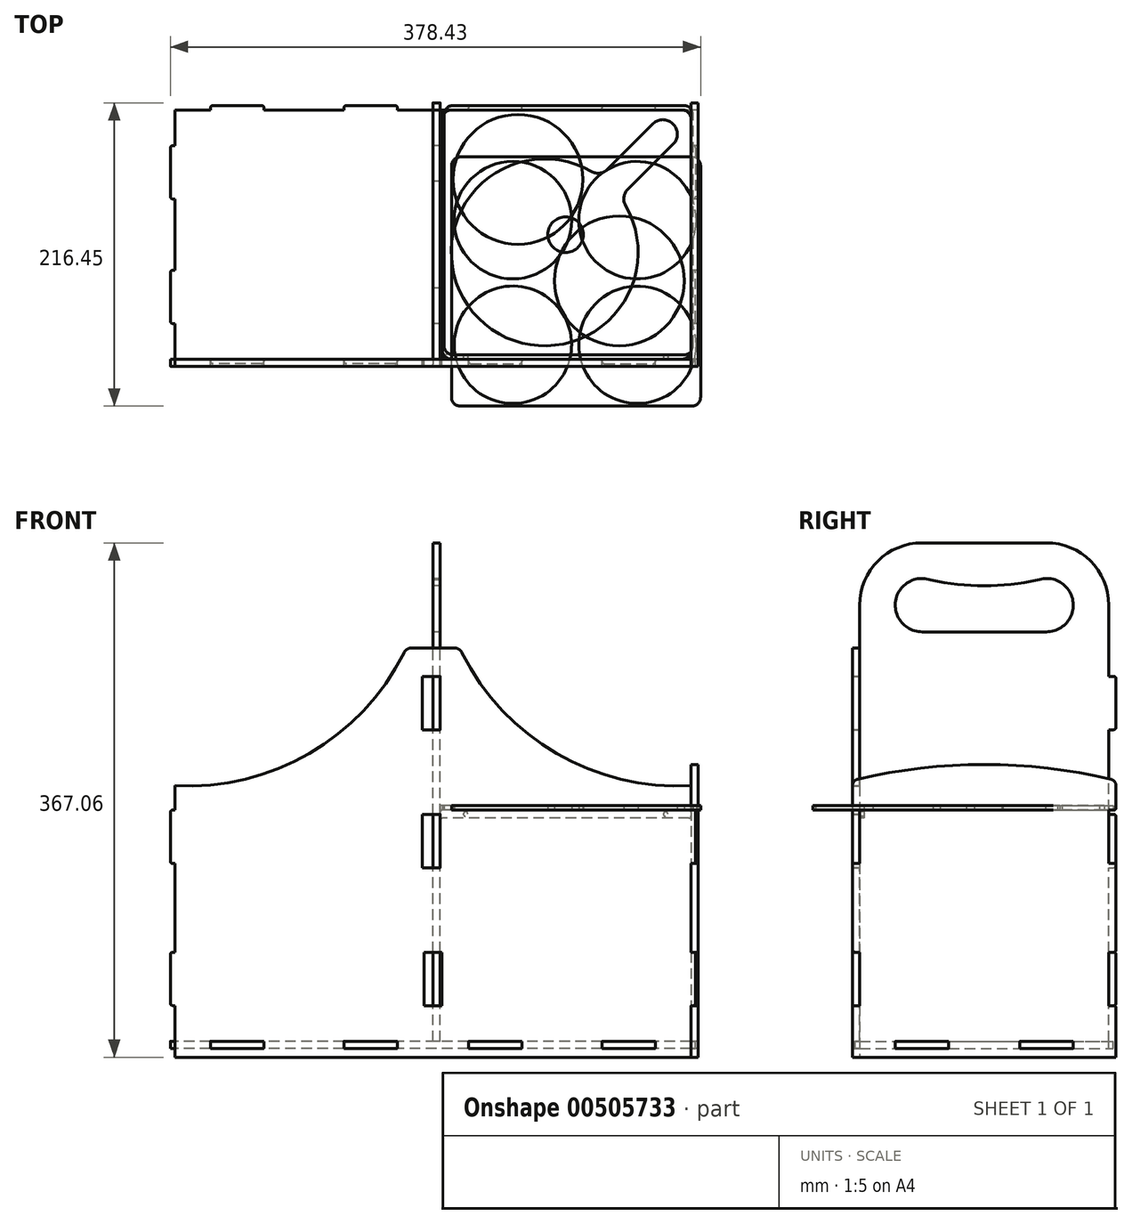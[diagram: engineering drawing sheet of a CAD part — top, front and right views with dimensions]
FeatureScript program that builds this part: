
annotation { "Feature Type Name" : "Feature", "Feature Type Description" : "" }
export const myFeature = defineFeature(function(context is Context, id is Id, definition is map)
    precondition{}
    {
        {
            var Q0;
            Q0=qCreatedBy(makeId("Right.planeOp"),FACE);
            var sketch = newSketch(context, id + "F0", { "sketchPlane" : qUnion([Q0])});
            skLineSegment(sketch, "E0.bottom", {"start": v(-88.9, 0) * mm, "end": v(88.9, 0) * mm});
            skLineSegment(sketch, "E0.top", {"start": v(-44.45, 355.6) * mm, "end": v(44.45, 355.6) * mm});
            skLineSegment(sketch, "E0.left", {"start": v(-88.9, 0) * mm, "end": v(-88.9, 25.4) * mm});
            skLineSegment(sketch, "E0.right", {"start": v(88.9, 0) * mm, "end": v(88.9, 25.4) * mm});
            skArc(sketch, "E1", {"start": v(-38.14, 329.13) * mm, "mid": v(-63.24, 314.26) * mm, "end": v(-44.27, 292.1) * mm});
            skArc(sketch, "E2", {"start": v(44.27, 292.1) * mm, "mid": v(63.24, 314.26) * mm, "end": v(38.14, 329.13) * mm});
            skPoint(sketch, "E3", {"position": v(-38.14, 329.13) * mm});
            skPoint(sketch, "E4", {"position": v(38.14, 329.13) * mm});
            skArc(sketch, "E5", {"start": v(-38.14, 329.13) * mm, "mid": v(0, 324.96) * mm, "end": v(38.14, 329.13) * mm});
            skLineSegment(sketch, "E6", {"start": v(-44.27, 292.1) * mm, "end": v(44.63, 292.1) * mm});
            skArc(sketch, "E7", {"start": v(88.9, 311.15) * mm, "mid": v(75.88, 342.58) * mm, "end": v(44.45, 355.6) * mm});
            skArc(sketch, "E8", {"start": v(-88.9, 311.15) * mm, "mid": v(-75.88, 342.58) * mm, "end": v(-44.45, 355.6) * mm});
            skLineSegment(sketch, "E9.top", {"start": v(94.01, 26.99) * mm, "end": v(94.01, 61.91) * mm});
            skLineSegment(sketch, "E9.left", {"start": v(88.9, 25.4) * mm, "end": v(92.42, 25.4) * mm});
            skLineSegment(sketch, "E9.right", {"start": v(88.9, 63.5) * mm, "end": v(92.42, 63.5) * mm});
            skPoint(sketch, "E10.visualSharp", {"position": v(94.01, 25.4) * mm});
            skArc(sketch, "E10.filletArc", {"start": v(92.42, 25.4) * mm, "mid": v(93.55, 25.86) * mm, "end": v(94.01, 26.99) * mm});
            skPoint(sketch, "E11.visualSharp", {"position": v(94.01, 63.5) * mm});
            skArc(sketch, "E11.filletArc", {"start": v(94.01, 61.91) * mm, "mid": v(93.55, 63.04) * mm, "end": v(92.42, 63.5) * mm});
            skLineSegment(sketch, "E12.top", {"start": v(94.01, 223.84) * mm, "end": v(94.01, 258.76) * mm});
            skLineSegment(sketch, "E12.left", {"start": v(88.9, 222.25) * mm, "end": v(92.42, 222.25) * mm});
            skLineSegment(sketch, "E12.right", {"start": v(88.9, 260.35) * mm, "end": v(92.42, 260.35) * mm});
            skPoint(sketch, "E13.visualSharp", {"position": v(94.01, 222.25) * mm});
            skArc(sketch, "E13.filletArc", {"start": v(92.42, 222.25) * mm, "mid": v(93.55, 222.71) * mm, "end": v(94.01, 223.84) * mm});
            skPoint(sketch, "E14.visualSharp", {"position": v(94.01, 260.35) * mm});
            skArc(sketch, "E14.filletArc", {"start": v(94.01, 258.76) * mm, "mid": v(93.55, 259.89) * mm, "end": v(92.42, 260.35) * mm});
            skLineSegment(sketch, "E15.top", {"start": v(94.01, 125.41) * mm, "end": v(94.01, 160.34) * mm});
            skLineSegment(sketch, "E15.left", {"start": v(88.9, 123.83) * mm, "end": v(92.42, 123.83) * mm});
            skLineSegment(sketch, "E15.right", {"start": v(88.9, 161.93) * mm, "end": v(92.42, 161.93) * mm});
            skPoint(sketch, "E16.visualSharp", {"position": v(94.01, 123.83) * mm});
            skArc(sketch, "E16.filletArc", {"start": v(92.42, 123.83) * mm, "mid": v(93.55, 124.29) * mm, "end": v(94.01, 125.41) * mm});
            skPoint(sketch, "E17.visualSharp", {"position": v(94.01, 161.93) * mm});
            skArc(sketch, "E17.filletArc", {"start": v(94.01, 160.34) * mm, "mid": v(93.55, 161.46) * mm, "end": v(92.42, 161.93) * mm});
            skArc(sketch, "E18.MirrorCS", {"start": v(-92.42, 25.4) * mm, "mid": v(-93.55, 25.86) * mm, "end": v(-94.01, 26.99) * mm});
            skLineSegment(sketch, "E19.MirrorCS", {"start": v(-88.9, 25.4) * mm, "end": v(-92.42, 25.4) * mm});
            skLineSegment(sketch, "E20.MirrorCS", {"start": v(-88.9, 161.93) * mm, "end": v(-92.42, 161.93) * mm});
            skArc(sketch, "E21.MirrorCS", {"start": v(-92.42, 222.25) * mm, "mid": v(-93.55, 222.71) * mm, "end": v(-94.01, 223.84) * mm});
            skArc(sketch, "E22.MirrorCS", {"start": v(-94.01, 258.76) * mm, "mid": v(-93.55, 259.89) * mm, "end": v(-92.42, 260.35) * mm});
            skLineSegment(sketch, "E23.MirrorCS", {"start": v(-88.9, 63.5) * mm, "end": v(-92.42, 63.5) * mm});
            skArc(sketch, "E24.MirrorCS", {"start": v(-94.01, 61.91) * mm, "mid": v(-93.55, 63.04) * mm, "end": v(-92.42, 63.5) * mm});
            skArc(sketch, "E25.MirrorCS", {"start": v(-94.01, 160.34) * mm, "mid": v(-93.55, 161.46) * mm, "end": v(-92.42, 161.93) * mm});
            skArc(sketch, "E26.MirrorCS", {"start": v(-92.42, 123.83) * mm, "mid": v(-93.55, 124.29) * mm, "end": v(-94.01, 125.41) * mm});
            skLineSegment(sketch, "E27.MirrorCS", {"start": v(-88.9, 222.25) * mm, "end": v(-92.42, 222.25) * mm});
            skLineSegment(sketch, "E28.MirrorCS", {"start": v(-88.9, 123.83) * mm, "end": v(-92.42, 123.83) * mm});
            skLineSegment(sketch, "E29.MirrorCS", {"start": v(-88.9, 260.35) * mm, "end": v(-92.42, 260.35) * mm});
            skPoint(sketch, "E30.MirrorP", {"position": v(-94.01, 260.35) * mm});
            skPoint(sketch, "E31.MirrorP", {"position": v(-94.01, 63.5) * mm});
            skPoint(sketch, "E32.MirrorP", {"position": v(-94.01, 25.4) * mm});
            skLineSegment(sketch, "E33.MirrorCS", {"start": v(-94.01, 125.41) * mm, "end": v(-94.01, 160.34) * mm});
            skPoint(sketch, "E34.MirrorP", {"position": v(-94.01, 161.93) * mm});
            skPoint(sketch, "E35.MirrorP", {"position": v(-94.01, 123.83) * mm});
            skPoint(sketch, "E36.MirrorP", {"position": v(-94.01, 222.25) * mm});
            skLineSegment(sketch, "E37.MirrorCS", {"start": v(-94.01, 223.84) * mm, "end": v(-94.01, 258.76) * mm});
            skLineSegment(sketch, "E38.MirrorCS", {"start": v(-94.01, 26.99) * mm, "end": v(-94.01, 61.91) * mm});
            skLineSegment(sketch, "E39.trimOffspring", {"start": v(88.9, 260.35) * mm, "end": v(88.9, 311.15) * mm});
            skLineSegment(sketch, "E40.trimOffspring", {"start": v(-88.9, 260.35) * mm, "end": v(-88.9, 311.15) * mm});
            skLineSegment(sketch, "E41.trimOffspring", {"start": v(-88.9, 161.93) * mm, "end": v(-88.9, 222.25) * mm});
            skLineSegment(sketch, "E42.trimOffspring", {"start": v(88.9, 161.93) * mm, "end": v(88.9, 222.25) * mm});
            skLineSegment(sketch, "E43.trimOffspring", {"start": v(-88.9, 63.5) * mm, "end": v(-88.9, 123.83) * mm});
            skLineSegment(sketch, "E44.trimOffspring", {"start": v(88.9, 63.5) * mm, "end": v(88.9, 123.83) * mm});
            skSolve(sketch);
        }
        {
            var Q0;
            Q0=makeQuery(id+"F0.imprint","IMPRINT",FACE,{"disambiguationData":[TD([[makeQuery(id+"F0.imprint","IMPRINT",EDGE,{"derivedFrom":sQuery(id+"F0.wireOp",EDGE,"E0.bottom")}),1.0]])]});
            extrude(context, id + "F1", {"entities" : qUnion([Q0]), "depth" : 5.11 * mm, "offsetDistance" : 25.4 * mm});
        }
        {
            var Q0;
            Q0=qCreatedBy(makeId("Top.planeOp"),FACE);
            var sketch = newSketch(context, id + "F2", { "sketchPlane" : qUnion([Q0])});
            skLineSegment(sketch, "E45.bottom", {"start": v(184.15, -88.9) * mm, "end": v(158.75, -88.9) * mm});
            skLineSegment(sketch, "E45.top", {"start": v(184.15, 88.9) * mm, "end": v(158.75, 88.9) * mm});
            skLineSegment(sketch, "E45.left", {"start": v(184.15, -88.9) * mm, "end": v(184.15, -63.5) * mm});
            skLineSegment(sketch, "E45.right", {"start": v(-184.15, -88.9) * mm, "end": v(-184.15, -63.5) * mm});
            skPoint(sketch, "E45.middle", {"position": v(0, 0) * mm});
            skLineSegment(sketch, "E46.top", {"start": v(26.99, -92.07) * mm, "end": v(61.91, -92.07) * mm});
            skLineSegment(sketch, "E46.left", {"start": v(25.4, -88.9) * mm, "end": v(25.4, -90.49) * mm});
            skLineSegment(sketch, "E46.right", {"start": v(63.5, -88.9) * mm, "end": v(63.5, -90.49) * mm});
            skPoint(sketch, "E47.visualSharp", {"position": v(25.4, -92.07) * mm});
            skArc(sketch, "E47.filletArc", {"start": v(25.4, -90.49) * mm, "mid": v(25.86, -91.61) * mm, "end": v(26.99, -92.07) * mm});
            skPoint(sketch, "E48.visualSharp", {"position": v(63.5, -92.07) * mm});
            skArc(sketch, "E48.filletArc", {"start": v(61.91, -92.08) * mm, "mid": v(63.04, -91.61) * mm, "end": v(63.5, -90.49) * mm});
            skLineSegment(sketch, "E49.top", {"start": v(122.24, -92.07) * mm, "end": v(157.16, -92.07) * mm});
            skLineSegment(sketch, "E49.left", {"start": v(120.65, -88.9) * mm, "end": v(120.65, -90.49) * mm});
            skLineSegment(sketch, "E49.right", {"start": v(158.75, -88.9) * mm, "end": v(158.75, -90.49) * mm});
            skPoint(sketch, "E50.visualSharp", {"position": v(120.65, -92.07) * mm});
            skArc(sketch, "E50.filletArc", {"start": v(120.65, -90.49) * mm, "mid": v(121.11, -91.61) * mm, "end": v(122.24, -92.07) * mm});
            skPoint(sketch, "E51.visualSharp", {"position": v(158.75, -92.07) * mm});
            skArc(sketch, "E51.filletArc", {"start": v(157.16, -92.08) * mm, "mid": v(158.29, -91.61) * mm, "end": v(158.75, -90.49) * mm});
            skLineSegment(sketch, "E52.top", {"start": v(187.33, -61.91) * mm, "end": v(187.33, -26.99) * mm});
            skLineSegment(sketch, "E52.left", {"start": v(184.15, -63.5) * mm, "end": v(185.74, -63.5) * mm});
            skLineSegment(sketch, "E52.right", {"start": v(184.15, -25.4) * mm, "end": v(185.74, -25.4) * mm});
            skPoint(sketch, "E53.visualSharp", {"position": v(187.33, -63.5) * mm});
            skArc(sketch, "E53.filletArc", {"start": v(185.74, -63.5) * mm, "mid": v(186.86, -63.04) * mm, "end": v(187.33, -61.91) * mm});
            skPoint(sketch, "E54.visualSharp", {"position": v(187.33, -25.4) * mm});
            skArc(sketch, "E54.filletArc", {"start": v(187.33, -26.99) * mm, "mid": v(186.86, -25.86) * mm, "end": v(185.74, -25.4) * mm});
            skLineSegment(sketch, "E55.MirrorCS", {"start": v(63.5, 88.9) * mm, "end": v(63.5, 90.49) * mm});
            skArc(sketch, "E56.MirrorCS", {"start": v(61.91, 92.08) * mm, "mid": v(63.04, 91.61) * mm, "end": v(63.5, 90.49) * mm});
            skLineSegment(sketch, "E57.MirrorCS", {"start": v(25.4, 88.9) * mm, "end": v(25.4, 90.49) * mm});
            skLineSegment(sketch, "E58.MirrorCS", {"start": v(120.65, 88.9) * mm, "end": v(120.65, 90.49) * mm});
            skLineSegment(sketch, "E59.MirrorCS", {"start": v(158.75, 88.9) * mm, "end": v(158.75, 90.49) * mm});
            skArc(sketch, "E60.MirrorCS", {"start": v(25.4, 90.49) * mm, "mid": v(25.86, 91.61) * mm, "end": v(26.99, 92.07) * mm});
            skArc(sketch, "E61.MirrorCS", {"start": v(157.16, 92.08) * mm, "mid": v(158.29, 91.61) * mm, "end": v(158.75, 90.49) * mm});
            skArc(sketch, "E62.MirrorCS", {"start": v(120.65, 90.49) * mm, "mid": v(121.11, 91.61) * mm, "end": v(122.24, 92.07) * mm});
            skLineSegment(sketch, "E63.MirrorCS", {"start": v(184.15, 25.4) * mm, "end": v(185.74, 25.4) * mm});
            skLineSegment(sketch, "E64.MirrorCS", {"start": v(184.15, 63.5) * mm, "end": v(185.74, 63.5) * mm});
            skArc(sketch, "E65.MirrorCS", {"start": v(187.33, 26.99) * mm, "mid": v(186.86, 25.86) * mm, "end": v(185.74, 25.4) * mm});
            skArc(sketch, "E66.MirrorCS", {"start": v(185.74, 63.5) * mm, "mid": v(186.86, 63.04) * mm, "end": v(187.33, 61.91) * mm});
            skPoint(sketch, "E67.MirrorP", {"position": v(158.75, 92.07) * mm});
            skLineSegment(sketch, "E68.MirrorCS", {"start": v(122.24, 92.07) * mm, "end": v(157.16, 92.07) * mm});
            skLineSegment(sketch, "E69.MirrorCS", {"start": v(26.99, 92.07) * mm, "end": v(61.91, 92.07) * mm});
            skLineSegment(sketch, "E70.MirrorCS", {"start": v(187.33, 61.91) * mm, "end": v(187.33, 26.99) * mm});
            skPoint(sketch, "E71.MirrorP", {"position": v(63.5, 92.07) * mm});
            skPoint(sketch, "E72.MirrorP", {"position": v(25.4, 92.07) * mm});
            skPoint(sketch, "E73.MirrorP", {"position": v(187.33, 63.5) * mm});
            skPoint(sketch, "E74.MirrorP", {"position": v(120.65, 92.07) * mm});
            skPoint(sketch, "E75.MirrorP", {"position": v(187.33, 25.4) * mm});
            skArc(sketch, "E76.MirrorCS", {"start": v(-120.65, -90.49) * mm, "mid": v(-121.11, -91.61) * mm, "end": v(-122.24, -92.07) * mm});
            skLineSegment(sketch, "E77.MirrorCS", {"start": v(-25.4, -88.9) * mm, "end": v(-25.4, -90.49) * mm});
            skLineSegment(sketch, "E78.MirrorCS", {"start": v(-120.65, -88.9) * mm, "end": v(-120.65, -90.49) * mm});
            skArc(sketch, "E79.MirrorCS", {"start": v(-61.91, -92.08) * mm, "mid": v(-63.04, -91.61) * mm, "end": v(-63.5, -90.49) * mm});
            skLineSegment(sketch, "E80.MirrorCS", {"start": v(-63.5, 88.9) * mm, "end": v(-63.5, 90.49) * mm});
            skLineSegment(sketch, "E81.MirrorCS", {"start": v(-158.75, -88.9) * mm, "end": v(-158.75, -90.49) * mm});
            skArc(sketch, "E82.MirrorCS", {"start": v(-120.65, 90.49) * mm, "mid": v(-121.11, 91.61) * mm, "end": v(-122.24, 92.07) * mm});
            skArc(sketch, "E83.MirrorCS", {"start": v(-25.4, -90.49) * mm, "mid": v(-25.86, -91.61) * mm, "end": v(-26.99, -92.07) * mm});
            skLineSegment(sketch, "E84.MirrorCS", {"start": v(-25.4, 88.9) * mm, "end": v(-25.4, 90.49) * mm});
            skArc(sketch, "E85.MirrorCS", {"start": v(-157.16, 92.08) * mm, "mid": v(-158.29, 91.61) * mm, "end": v(-158.75, 90.49) * mm});
            skArc(sketch, "E86.MirrorCS", {"start": v(-61.91, 92.08) * mm, "mid": v(-63.04, 91.61) * mm, "end": v(-63.5, 90.49) * mm});
            skLineSegment(sketch, "E87.MirrorCS", {"start": v(-120.65, 88.9) * mm, "end": v(-120.65, 90.49) * mm});
            skLineSegment(sketch, "E88.MirrorCS", {"start": v(-63.5, -88.9) * mm, "end": v(-63.5, -90.49) * mm});
            skArc(sketch, "E89.MirrorCS", {"start": v(-25.4, 90.49) * mm, "mid": v(-25.86, 91.61) * mm, "end": v(-26.99, 92.07) * mm});
            skLineSegment(sketch, "E90.MirrorCS", {"start": v(-158.75, 88.9) * mm, "end": v(-158.75, 90.49) * mm});
            skArc(sketch, "E91.MirrorCS", {"start": v(-157.16, -92.08) * mm, "mid": v(-158.29, -91.61) * mm, "end": v(-158.75, -90.49) * mm});
            skLineSegment(sketch, "E92.MirrorCS", {"start": v(-184.15, 25.4) * mm, "end": v(-185.74, 25.4) * mm});
            skLineSegment(sketch, "E93.MirrorCS", {"start": v(-184.15, -63.5) * mm, "end": v(-185.74, -63.5) * mm});
            skLineSegment(sketch, "E94.MirrorCS", {"start": v(-184.15, -25.4) * mm, "end": v(-185.74, -25.4) * mm});
            skArc(sketch, "E95.MirrorCS", {"start": v(-187.33, -26.99) * mm, "mid": v(-186.86, -25.86) * mm, "end": v(-185.74, -25.4) * mm});
            skArc(sketch, "E96.MirrorCS", {"start": v(-187.33, 26.99) * mm, "mid": v(-186.86, 25.86) * mm, "end": v(-185.74, 25.4) * mm});
            skArc(sketch, "E97.MirrorCS", {"start": v(-185.74, 63.5) * mm, "mid": v(-186.86, 63.04) * mm, "end": v(-187.33, 61.91) * mm});
            skLineSegment(sketch, "E98.MirrorCS", {"start": v(-184.15, 63.5) * mm, "end": v(-185.74, 63.5) * mm});
            skArc(sketch, "E99.MirrorCS", {"start": v(-185.74, -63.5) * mm, "mid": v(-186.86, -63.04) * mm, "end": v(-187.33, -61.91) * mm});
            skPoint(sketch, "E100.MirrorP", {"position": v(-25.4, -92.07) * mm});
            skLineSegment(sketch, "E101.MirrorCS", {"start": v(-122.24, -92.07) * mm, "end": v(-157.16, -92.07) * mm});
            skPoint(sketch, "E102.MirrorP", {"position": v(-158.75, -92.07) * mm});
            skPoint(sketch, "E103.MirrorP", {"position": v(-120.65, 92.07) * mm});
            skPoint(sketch, "E104.MirrorP", {"position": v(-120.65, -92.07) * mm});
            skLineSegment(sketch, "E105.MirrorCS", {"start": v(-122.24, 92.07) * mm, "end": v(-157.16, 92.07) * mm});
            skLineSegment(sketch, "E106.MirrorCS", {"start": v(-26.99, -92.07) * mm, "end": v(-61.91, -92.07) * mm});
            skPoint(sketch, "E107.MirrorP", {"position": v(-63.5, 92.07) * mm});
            skLineSegment(sketch, "E108.MirrorCS", {"start": v(-26.99, 92.07) * mm, "end": v(-61.91, 92.07) * mm});
            skPoint(sketch, "E109.MirrorP", {"position": v(-158.75, 92.07) * mm});
            skPoint(sketch, "E110.MirrorP", {"position": v(-63.5, -92.07) * mm});
            skPoint(sketch, "E111.MirrorP", {"position": v(-25.4, 92.07) * mm});
            skPoint(sketch, "E112.MirrorP", {"position": v(-187.33, -25.4) * mm});
            skLineSegment(sketch, "E113.MirrorCS", {"start": v(-187.33, 61.91) * mm, "end": v(-187.33, 26.99) * mm});
            skPoint(sketch, "E114.MirrorP", {"position": v(-187.33, -63.5) * mm});
            skPoint(sketch, "E115.MirrorP", {"position": v(-187.33, 63.5) * mm});
            skLineSegment(sketch, "E116.MirrorCS", {"start": v(-187.33, -61.91) * mm, "end": v(-187.33, -26.99) * mm});
            skPoint(sketch, "E117.MirrorP", {"position": v(-187.33, 25.4) * mm});
            skLineSegment(sketch, "E118.trimOffspring", {"start": v(-184.15, -25.4) * mm, "end": v(-184.15, 25.4) * mm});
            skLineSegment(sketch, "E119.trimOffspring", {"start": v(120.65, -88.9) * mm, "end": v(63.5, -88.9) * mm});
            skLineSegment(sketch, "E120.trimOffspring", {"start": v(25.4, -88.9) * mm, "end": v(-25.4, -88.9) * mm});
            skLineSegment(sketch, "E121.trimOffspring", {"start": v(184.15, -25.4) * mm, "end": v(184.15, 25.4) * mm});
            skLineSegment(sketch, "E122.trimOffspring", {"start": v(184.15, 63.5) * mm, "end": v(184.15, 88.9) * mm});
            skLineSegment(sketch, "E123.trimOffspring", {"start": v(120.65, 88.9) * mm, "end": v(63.5, 88.9) * mm});
            skLineSegment(sketch, "E124.trimOffspring", {"start": v(25.4, 88.9) * mm, "end": v(-25.4, 88.9) * mm});
            skLineSegment(sketch, "E125.trimOffspring", {"start": v(-63.5, 88.9) * mm, "end": v(-120.65, 88.9) * mm});
            skLineSegment(sketch, "E126.trimOffspring", {"start": v(-158.75, 88.9) * mm, "end": v(-184.15, 88.9) * mm});
            skLineSegment(sketch, "E127.trimOffspring", {"start": v(-184.15, 63.5) * mm, "end": v(-184.15, 88.9) * mm});
            skLineSegment(sketch, "E128.trimOffspring", {"start": v(-63.5, -88.9) * mm, "end": v(-120.65, -88.9) * mm});
            skLineSegment(sketch, "E129.trimOffspring", {"start": v(-158.75, -88.9) * mm, "end": v(-184.15, -88.9) * mm});
            skSolve(sketch);
        }
        {
            var Q0;
            Q0 = qSketchRegion(id + "F2", true);
            extrude(context, id + "F3", {"entities" : qUnion([Q0]), "oppositeDirection" : true, "depth" : 5.11 * mm, "offsetDistance" : 25.4 * mm});
        }
        {
            var Q0;
            Q0=makeQuery(id+"F1.opExtrude","SWEPT_FACE",FACE,{"disambiguationData":[OSD([sQuery(id+"F0.wireOp",EDGE,"E41.trimOffspring")])]});
            var sketch = newSketch(context, id + "F4", { "sketchPlane" : qUnion([Q0])});
            skLineSegment(sketch, "E130.bottom", {"start": v(-184.15, -11.46) * mm, "end": v(184.25, -11.46) * mm});
            skLineSegment(sketch, "E130.top", {"start": v(-15.07, 280.64) * mm, "end": v(15.07, 280.64) * mm});
            skLineSegment(sketch, "E131.bottom", {"start": v(5.11, 260.35) * mm, "end": v(-7.59, 260.35) * mm});
            skLineSegment(sketch, "E131.top", {"start": v(5.11, 222.25) * mm, "end": v(-7.59, 222.25) * mm});
            skLineSegment(sketch, "E131.left", {"start": v(5.11, 260.35) * mm, "end": v(5.11, 222.25) * mm});
            skLineSegment(sketch, "E131.right", {"start": v(-7.59, 260.35) * mm, "end": v(-7.59, 222.25) * mm});
            skLineSegment(sketch, "E132.bottom", {"start": v(5.11, 161.93) * mm, "end": v(-7.6, 161.93) * mm});
            skLineSegment(sketch, "E132.top", {"start": v(5.11, 123.83) * mm, "end": v(-7.59, 123.83) * mm});
            skLineSegment(sketch, "E132.left", {"start": v(5.11, 161.93) * mm, "end": v(5.11, 123.83) * mm});
            skLineSegment(sketch, "E132.right", {"start": v(-7.6, 161.93) * mm, "end": v(-7.59, 123.83) * mm});
            skLineSegment(sketch, "E133.bottom", {"start": v(6.33, 63.5) * mm, "end": v(-6.37, 63.5) * mm});
            skLineSegment(sketch, "E133.top", {"start": v(6.33, 25.4) * mm, "end": v(-6.37, 25.4) * mm});
            skLineSegment(sketch, "E133.left", {"start": v(6.33, 63.5) * mm, "end": v(6.33, 25.4) * mm});
            skLineSegment(sketch, "E133.right", {"start": v(-6.37, 63.5) * mm, "end": v(-6.37, 25.4) * mm});
            skLineSegment(sketch, "E134.bottom", {"start": v(25.4, 0) * mm, "end": v(63.5, 0) * mm});
            skLineSegment(sketch, "E134.top", {"start": v(25.4, -5.11) * mm, "end": v(63.5, -5.11) * mm});
            skLineSegment(sketch, "E134.left", {"start": v(25.4, 0) * mm, "end": v(25.4, -5.1) * mm});
            skLineSegment(sketch, "E134.right", {"start": v(63.5, 0) * mm, "end": v(63.5, -5.11) * mm});
            skLineSegment(sketch, "E135.bottom", {"start": v(120.65, 0) * mm, "end": v(158.75, 0) * mm});
            skLineSegment(sketch, "E135.top", {"start": v(120.65, -5.11) * mm, "end": v(158.75, -5.11) * mm});
            skLineSegment(sketch, "E135.left", {"start": v(120.65, 0) * mm, "end": v(120.65, -5.11) * mm});
            skLineSegment(sketch, "E135.right", {"start": v(158.75, 0) * mm, "end": v(158.75, -5.11) * mm});
            skLineSegment(sketch, "E136.MirrorCS", {"start": v(-120.65, 0) * mm, "end": v(-120.65, -5.11) * mm});
            skLineSegment(sketch, "E137.MirrorCS", {"start": v(-158.75, 0) * mm, "end": v(-158.75, -5.11) * mm});
            skLineSegment(sketch, "E138.MirrorCS", {"start": v(-120.65, -5.11) * mm, "end": v(-158.75, -5.11) * mm});
            skLineSegment(sketch, "E139.MirrorCS", {"start": v(-120.65, 0) * mm, "end": v(-158.75, 0) * mm});
            skLineSegment(sketch, "E140.MirrorCS", {"start": v(-63.5, 0) * mm, "end": v(-63.5, -5.11) * mm});
            skLineSegment(sketch, "E141.MirrorCS", {"start": v(-25.4, 0) * mm, "end": v(-25.4, -5.1) * mm});
            skLineSegment(sketch, "E142.MirrorCS", {"start": v(-25.4, 0) * mm, "end": v(-63.5, 0) * mm});
            skLineSegment(sketch, "E143.MirrorCS", {"start": v(-25.4, -5.1) * mm, "end": v(-63.5, -5.11) * mm});
            skLineSegment(sketch, "E144", {"start": v(184.25, 182.32) * mm, "end": v(184.25, 164.86) * mm});
            skLineSegment(sketch, "E145.bottom", {"start": v(184.25, 63.5) * mm, "end": v(185.84, 63.5) * mm});
            skLineSegment(sketch, "E145.top", {"start": v(184.25, 25.4) * mm, "end": v(185.84, 25.4) * mm});
            skLineSegment(sketch, "E145.right", {"start": v(187.43, 61.91) * mm, "end": v(187.43, 26.99) * mm});
            skLineSegment(sketch, "E146.bottom", {"start": v(184.25, 164.86) * mm, "end": v(185.84, 164.86) * mm});
            skLineSegment(sketch, "E146.top", {"start": v(184.25, 126.76) * mm, "end": v(185.84, 126.76) * mm});
            skLineSegment(sketch, "E146.right", {"start": v(187.43, 163.27) * mm, "end": v(187.43, 128.35) * mm});
            skPoint(sketch, "E147.visualSharp", {"position": v(187.43, 164.86) * mm});
            skArc(sketch, "E147.filletArc", {"start": v(187.43, 163.27) * mm, "mid": v(186.96, 164.4) * mm, "end": v(185.84, 164.86) * mm});
            skPoint(sketch, "E148.visualSharp", {"position": v(187.43, 126.76) * mm});
            skArc(sketch, "E148.filletArc", {"start": v(185.84, 126.76) * mm, "mid": v(186.96, 127.22) * mm, "end": v(187.43, 128.35) * mm});
            skPoint(sketch, "E149.visualSharp", {"position": v(187.43, 63.5) * mm});
            skArc(sketch, "E149.filletArc", {"start": v(187.43, 61.91) * mm, "mid": v(186.96, 63.04) * mm, "end": v(185.84, 63.5) * mm});
            skPoint(sketch, "E150.visualSharp", {"position": v(187.43, 25.4) * mm});
            skArc(sketch, "E150.filletArc", {"start": v(185.84, 25.4) * mm, "mid": v(186.96, 25.86) * mm, "end": v(187.43, 26.99) * mm});
            skArc(sketch, "E151.MirrorCS", {"start": v(-185.84, 126.76) * mm, "mid": v(-186.96, 127.22) * mm, "end": v(-187.43, 128.35) * mm});
            skLineSegment(sketch, "E152.MirrorCS", {"start": v(-184.25, 126.76) * mm, "end": v(-185.84, 126.76) * mm});
            skLineSegment(sketch, "E153.MirrorCS", {"start": v(-184.25, 164.86) * mm, "end": v(-185.84, 164.86) * mm});
            skArc(sketch, "E154.MirrorCS", {"start": v(-185.84, 25.4) * mm, "mid": v(-186.96, 25.86) * mm, "end": v(-187.43, 26.99) * mm});
            skLineSegment(sketch, "E155.MirrorCS", {"start": v(-184.25, 63.5) * mm, "end": v(-185.84, 63.5) * mm});
            skArc(sketch, "E156.MirrorCS", {"start": v(-187.43, 163.27) * mm, "mid": v(-186.96, 164.4) * mm, "end": v(-185.84, 164.86) * mm});
            skArc(sketch, "E157.MirrorCS", {"start": v(-187.43, 61.91) * mm, "mid": v(-186.96, 63.04) * mm, "end": v(-185.84, 63.5) * mm});
            skLineSegment(sketch, "E158.MirrorCS", {"start": v(-184.25, 25.4) * mm, "end": v(-185.84, 25.4) * mm});
            skPoint(sketch, "E159.MirrorP", {"position": v(-187.43, 25.4) * mm});
            skPoint(sketch, "E160.MirrorP", {"position": v(-187.43, 164.86) * mm});
            skPoint(sketch, "E161.MirrorP", {"position": v(-187.43, 126.76) * mm});
            skPoint(sketch, "E162.MirrorP", {"position": v(-187.43, 63.5) * mm});
            skLineSegment(sketch, "E163.MirrorCS", {"start": v(-187.43, 61.91) * mm, "end": v(-187.43, 26.99) * mm});
            skLineSegment(sketch, "E164.MirrorCS", {"start": v(-187.43, 163.27) * mm, "end": v(-187.43, 128.35) * mm});
            skLineSegment(sketch, "E165.trimOffspring", {"start": v(184.25, 126.76) * mm, "end": v(184.25, 63.5) * mm});
            skLineSegment(sketch, "E166.trimOffspring", {"start": v(184.25, 25.4) * mm, "end": v(184.25, -11.46) * mm});
            skLineSegment(sketch, "E167", {"start": v(-184.25, 182.32) * mm, "end": v(-184.25, 164.86) * mm});
            skLineSegment(sketch, "E168", {"start": v(-184.25, 126.76) * mm, "end": v(-184.25, 63.5) * mm});
            skLineSegment(sketch, "E169", {"start": v(-184.25, 25.4) * mm, "end": v(-184.15, -11.46) * mm});
            skPoint(sketch, "E170", {"position": v(19.05, 280.64) * mm});
            skPoint(sketch, "E171", {"position": v(184.25, 182.32) * mm});
            skArc(sketch, "E172", {"start": v(20.75, 277.13) * mm, "mid": v(88.3, 205.23) * mm, "end": v(184.25, 182.32) * mm});
            skArc(sketch, "E173.MirrorCS", {"start": v(-20.75, 277.13) * mm, "mid": v(-88.3, 205.23) * mm, "end": v(-184.25, 182.32) * mm});
            skPoint(sketch, "E174.visualSharp", {"position": v(-19.05, 280.64) * mm});
            skArc(sketch, "E174.filletArc", {"start": v(-15.07, 280.64) * mm, "mid": v(-18.41, 279.7) * mm, "end": v(-20.75, 277.13) * mm});
            skArc(sketch, "E175.filletArc", {"start": v(20.75, 277.13) * mm, "mid": v(18.41, 279.7) * mm, "end": v(15.07, 280.64) * mm});
            skLineSegment(sketch, "E176", {"start": v(184.25, 164.86) * mm, "end": v(-184.25, 164.86) * mm, "construction": true});
            skSolve(sketch);
        }
        {
            var Q0;
            Q0 = qSketchRegion(id + "F4", true);
            extrude(context, id + "F5", {"entities" : qUnion([Q0]), "depth" : 5.11 * mm, "offsetDistance" : 25.4 * mm});
        }
        {
            var Q0;
            Q0=makeQuery(id+"F5.opExtrude","SWEPT_FACE",FACE,{"disambiguationData":[OSD([sQuery(id+"F4.wireOp",EDGE,"E165.trimOffspring")])]});
            var sketch = newSketch(context, id + "F6", { "sketchPlane" : qUnion([Q0])});
            skLineSegment(sketch, "E177.bottom", {"start": v(-94.01, -11.46) * mm, "end": v(94.01, -11.46) * mm});
            skLineSegment(sketch, "E177.left", {"start": v(-94.01, -11.46) * mm, "end": v(-94.01, 23.81) * mm});
            skLineSegment(sketch, "E177.right", {"start": v(94.01, -11.46) * mm, "end": v(94.01, 23.81) * mm});
            skArc(sketch, "E178", {"start": v(90.34, 186.95) * mm, "mid": v(0, 197.46) * mm, "end": v(-90.34, 186.95) * mm});
            skPoint(sketch, "E179.visualSharp", {"position": v(-94.01, 186.07) * mm});
            skArc(sketch, "E179.filletArc", {"start": v(-90.34, 186.95) * mm, "mid": v(-92.98, 185.27) * mm, "end": v(-94.01, 182.32) * mm});
            skPoint(sketch, "E180.visualSharp", {"position": v(94, 186.07) * mm});
            skArc(sketch, "E180.filletArc", {"start": v(94.01, 182.32) * mm, "mid": v(92.98, 185.27) * mm, "end": v(90.34, 186.95) * mm});
            skLineSegment(sketch, "E181.bottom", {"start": v(-92.42, 164.86) * mm, "end": v(-88.9, 164.86) * mm});
            skLineSegment(sketch, "E181.top", {"start": v(-92.42, 126.76) * mm, "end": v(-88.9, 126.76) * mm});
            skLineSegment(sketch, "E181.right", {"start": v(-88.9, 164.86) * mm, "end": v(-88.9, 126.76) * mm});
            skLineSegment(sketch, "E182.trimOffspring", {"start": v(-94.01, 166.45) * mm, "end": v(-94.01, 182.32) * mm});
            skPoint(sketch, "E183.visualSharp", {"position": v(-94, 164.86) * mm});
            skArc(sketch, "E183.filletArc", {"start": v(-94.01, 166.45) * mm, "mid": v(-93.55, 165.32) * mm, "end": v(-92.42, 164.86) * mm});
            skPoint(sketch, "E184.visualSharp", {"position": v(-94, 126.76) * mm});
            skArc(sketch, "E184.filletArc", {"start": v(-92.42, 126.76) * mm, "mid": v(-93.55, 126.3) * mm, "end": v(-94.01, 125.17) * mm});
            skLineSegment(sketch, "E185.bottom", {"start": v(-92.42, 63.5) * mm, "end": v(-88.9, 63.5) * mm});
            skLineSegment(sketch, "E185.top", {"start": v(-92.42, 25.4) * mm, "end": v(-88.9, 25.4) * mm});
            skLineSegment(sketch, "E185.right", {"start": v(-88.9, 63.5) * mm, "end": v(-88.9, 25.4) * mm});
            skLineSegment(sketch, "E186.trimOffspring", {"start": v(-94.01, 65.09) * mm, "end": v(-94.01, 125.17) * mm});
            skPoint(sketch, "E187.visualSharp", {"position": v(-94, 25.4) * mm});
            skArc(sketch, "E187.filletArc", {"start": v(-92.42, 25.4) * mm, "mid": v(-93.55, 24.94) * mm, "end": v(-94.01, 23.81) * mm});
            skPoint(sketch, "E188.visualSharp", {"position": v(-94.01, 63.5) * mm});
            skArc(sketch, "E188.filletArc", {"start": v(-94.01, 65.09) * mm, "mid": v(-93.55, 63.96) * mm, "end": v(-92.42, 63.5) * mm});
            skLineSegment(sketch, "E189.MirrorCS", {"start": v(92.42, 164.86) * mm, "end": v(88.9, 164.86) * mm});
            skArc(sketch, "E190.MirrorCS", {"start": v(94.01, 166.45) * mm, "mid": v(93.55, 165.32) * mm, "end": v(92.42, 164.86) * mm});
            skLineSegment(sketch, "E191.MirrorCS", {"start": v(92.42, 63.5) * mm, "end": v(88.9, 63.5) * mm});
            skLineSegment(sketch, "E192.MirrorCS", {"start": v(92.42, 126.76) * mm, "end": v(88.9, 126.76) * mm});
            skArc(sketch, "E193.MirrorCS", {"start": v(92.42, 126.76) * mm, "mid": v(93.55, 126.3) * mm, "end": v(94.01, 125.17) * mm});
            skArc(sketch, "E194.MirrorCS", {"start": v(92.42, 25.4) * mm, "mid": v(93.55, 24.94) * mm, "end": v(94.01, 23.81) * mm});
            skArc(sketch, "E195.MirrorCS", {"start": v(94.01, 65.09) * mm, "mid": v(93.55, 63.96) * mm, "end": v(92.42, 63.5) * mm});
            skLineSegment(sketch, "E196.MirrorCS", {"start": v(92.42, 25.4) * mm, "end": v(88.9, 25.4) * mm});
            skLineSegment(sketch, "E197.MirrorCS", {"start": v(94.01, 65.09) * mm, "end": v(94.01, 125.17) * mm});
            skLineSegment(sketch, "E198.MirrorCS", {"start": v(88.9, 63.5) * mm, "end": v(88.9, 25.4) * mm});
            skPoint(sketch, "E199.MirrorP", {"position": v(94, 25.4) * mm});
            skPoint(sketch, "E200.MirrorP", {"position": v(94.01, 63.5) * mm});
            skPoint(sketch, "E201.MirrorP", {"position": v(94, 164.86) * mm});
            skPoint(sketch, "E202.MirrorP", {"position": v(94, 126.76) * mm});
            skLineSegment(sketch, "E203.MirrorCS", {"start": v(88.9, 164.86) * mm, "end": v(88.9, 126.76) * mm});
            skLineSegment(sketch, "E204.trimOffspring", {"start": v(94, 166.45) * mm, "end": v(94, 182.32) * mm});
            skLineSegment(sketch, "E205.trimOffspring", {"start": v(94, 65.09) * mm, "end": v(94, 125.17) * mm});
            skLineSegment(sketch, "E206.bottom", {"start": v(-63.5, 0) * mm, "end": v(-25.4, 0) * mm});
            skLineSegment(sketch, "E206.top", {"start": v(-63.5, -5.11) * mm, "end": v(-25.4, -5.11) * mm});
            skLineSegment(sketch, "E206.left", {"start": v(-63.5, 0) * mm, "end": v(-63.5, -5.11) * mm});
            skLineSegment(sketch, "E206.right", {"start": v(-25.4, 0) * mm, "end": v(-25.4, -5.11) * mm});
            skLineSegment(sketch, "E207.MirrorCS", {"start": v(63.5, 0) * mm, "end": v(63.5, -5.11) * mm});
            skLineSegment(sketch, "E208.MirrorCS", {"start": v(63.5, 0) * mm, "end": v(25.4, 0) * mm});
            skLineSegment(sketch, "E209.MirrorCS", {"start": v(63.5, -5.11) * mm, "end": v(25.4, -5.11) * mm});
            skLineSegment(sketch, "E210.MirrorCS", {"start": v(25.4, 0) * mm, "end": v(25.4, -5.11) * mm});
            skSolve(sketch);
        }
        {
            var Q0;
            Q0 = qSketchRegion(id + "F6", true);
            extrude(context, id + "F7", {"entities" : qUnion([Q0]), "depth" : 5.11 * mm, "offsetDistance" : 25.4 * mm});
        }
        {
            var Q0;
            Q0=makeQuery(id+"F5.opExtrude","CAP_FACE",FACE,{"disambiguationData":[OSD([sQuery(id+"F4.wireOp",EDGE,"E130.bottom"),sQuery(id+"F4.wireOp",EDGE,"E130.top"),sQuery(id+"F4.wireOp",EDGE,"E131.bottom"),sQuery(id+"F4.wireOp",EDGE,"E131.top"),sQuery(id+"F4.wireOp",EDGE,"E131.left"),sQuery(id+"F4.wireOp",EDGE,"E131.right"),sQuery(id+"F4.wireOp",EDGE,"E132.bottom"),sQuery(id+"F4.wireOp",EDGE,"E132.top"),sQuery(id+"F4.wireOp",EDGE,"E132.left"),sQuery(id+"F4.wireOp",EDGE,"E132.right"),sQuery(id+"F4.wireOp",EDGE,"E133.bottom"),sQuery(id+"F4.wireOp",EDGE,"E133.top"),sQuery(id+"F4.wireOp",EDGE,"E133.left"),sQuery(id+"F4.wireOp",EDGE,"E133.right"),sQuery(id+"F4.wireOp",EDGE,"E134.bottom"),sQuery(id+"F4.wireOp",EDGE,"E134.top"),sQuery(id+"F4.wireOp",EDGE,"E134.left"),sQuery(id+"F4.wireOp",EDGE,"E134.right"),sQuery(id+"F4.wireOp",EDGE,"E135.bottom"),sQuery(id+"F4.wireOp",EDGE,"E135.top"),sQuery(id+"F4.wireOp",EDGE,"E135.left"),sQuery(id+"F4.wireOp",EDGE,"E135.right"),sQuery(id+"F4.wireOp",EDGE,"E136.MirrorCS"),sQuery(id+"F4.wireOp",EDGE,"E137.MirrorCS"),sQuery(id+"F4.wireOp",EDGE,"E138.MirrorCS"),sQuery(id+"F4.wireOp",EDGE,"E139.MirrorCS"),sQuery(id+"F4.wireOp",EDGE,"E140.MirrorCS"),sQuery(id+"F4.wireOp",EDGE,"E141.MirrorCS"),sQuery(id+"F4.wireOp",EDGE,"E142.MirrorCS"),sQuery(id+"F4.wireOp",EDGE,"E143.MirrorCS"),sQuery(id+"F4.wireOp",EDGE,"E144"),sQuery(id+"F4.wireOp",EDGE,"E145.bottom"),sQuery(id+"F4.wireOp",EDGE,"E145.top"),sQuery(id+"F4.wireOp",EDGE,"E145.right"),sQuery(id+"F4.wireOp",EDGE,"E146.bottom"),sQuery(id+"F4.wireOp",EDGE,"E146.top"),sQuery(id+"F4.wireOp",EDGE,"E146.right"),sQuery(id+"F4.wireOp",EDGE,"E147.filletArc"),sQuery(id+"F4.wireOp",EDGE,"E148.filletArc"),sQuery(id+"F4.wireOp",EDGE,"E149.filletArc"),sQuery(id+"F4.wireOp",EDGE,"E150.filletArc"),sQuery(id+"F4.wireOp",EDGE,"E151.MirrorCS"),sQuery(id+"F4.wireOp",EDGE,"E152.MirrorCS"),sQuery(id+"F4.wireOp",EDGE,"E153.MirrorCS"),sQuery(id+"F4.wireOp",EDGE,"E154.MirrorCS"),sQuery(id+"F4.wireOp",EDGE,"E155.MirrorCS"),sQuery(id+"F4.wireOp",EDGE,"E156.MirrorCS"),sQuery(id+"F4.wireOp",EDGE,"E157.MirrorCS"),sQuery(id+"F4.wireOp",EDGE,"E158.MirrorCS"),sQuery(id+"F4.wireOp",EDGE,"E163.MirrorCS"),sQuery(id+"F4.wireOp",EDGE,"E164.MirrorCS"),sQuery(id+"F4.wireOp",EDGE,"E165.trimOffspring"),sQuery(id+"F4.wireOp",EDGE,"E166.trimOffspring"),sQuery(id+"F4.wireOp",EDGE,"E167"),sQuery(id+"F4.wireOp",EDGE,"E168"),sQuery(id+"F4.wireOp",EDGE,"E169"),sQuery(id+"F4.wireOp",EDGE,"E172"),sQuery(id+"F4.wireOp",EDGE,"E173.MirrorCS"),sQuery(id+"F4.wireOp",EDGE,"E174.filletArc"),sQuery(id+"F4.wireOp",EDGE,"E175.filletArc")])],"isStart":true});
            var sketch = newSketch(context, id + "F8", { "sketchPlane" : qUnion([Q0])});
            skLineSegment(sketch, "E211.bottom", {"start": v(-182.66, 164.86) * mm, "end": v(-6.7, 164.86) * mm});
            skLineSegment(sketch, "E211.top", {"start": v(-182.66, 159.14) * mm, "end": v(-6.7, 159.14) * mm});
            skLineSegment(sketch, "E211.left", {"start": v(-184.25, 163.27) * mm, "end": v(-184.25, 160.73) * mm});
            skLineSegment(sketch, "E211.right", {"start": v(-5.11, 163.27) * mm, "end": v(-5.11, 160.73) * mm});
            skPoint(sketch, "E212.visualSharp", {"position": v(-184.25, 164.86) * mm});
            skArc(sketch, "E212.filletArc", {"start": v(-182.66, 164.86) * mm, "mid": v(-183.79, 164.4) * mm, "end": v(-184.25, 163.27) * mm});
            skPoint(sketch, "E213.visualSharp", {"position": v(-184.25, 159.14) * mm});
            skArc(sketch, "E213.filletArc", {"start": v(-184.25, 160.73) * mm, "mid": v(-183.79, 159.6) * mm, "end": v(-182.66, 159.14) * mm});
            skPoint(sketch, "E214.visualSharp", {"position": v(-5.11, 164.86) * mm});
            skArc(sketch, "E214.filletArc", {"start": v(-5.11, 163.27) * mm, "mid": v(-5.57, 164.4) * mm, "end": v(-6.7, 164.86) * mm});
            skPoint(sketch, "E215.visualSharp", {"position": v(-5.11, 159.14) * mm});
            skArc(sketch, "E215.filletArc", {"start": v(-6.7, 159.14) * mm, "mid": v(-5.57, 159.6) * mm, "end": v(-5.11, 160.73) * mm});
            skCircle(sketch, "E216", {"center": v(-166.05, 162) * mm, "radius": 1.59 * mm});
            skPoint(sketch, "E216.centerSnap0", {"position": v(-94.68, 164.86) * mm});
            skCircle(sketch, "E217", {"center": v(-23.3, 162) * mm, "radius": 1.59 * mm});
            skLineSegment(sketch, "E218", {"start": v(-94.68, 164.86) * mm, "end": v(-94.68, 159.14) * mm, "construction": true});
            skLineSegment(sketch, "E219", {"start": v(-166.05, 162) * mm, "end": v(-23.3, 162) * mm, "construction": true});
            skCircle(sketch, "E220", {"center": v(-94.68, 162) * mm, "radius": 1.59 * mm, "construction": true});
            skSolve(sketch);
        }
        {
            var Q0;
            Q0 = qSketchRegion(id + "F8", true);
            extrude(context, id + "F9", {"entities" : qUnion([Q0]), "depth" : 3.17 * mm});
        }
        {
            var Q0;
            Q0=makeQuery(id+"F9.opExtrude","SWEPT_FACE",FACE,{"disambiguationData":[OSD([sQuery(id+"F8.wireOp",EDGE,"E211.bottom")])]});
            var sketch = newSketch(context, id + "F10", { "sketchPlane" : qUnion([Q0])});
            skLineSegment(sketch, "E221", {"start": v(94.68, -85.73) * mm, "end": v(94.68, 98.75) * mm, "construction": true});
            skPoint(sketch, "E221.endSnap0", {"position": v(94.68, -85.73) * mm});
            skLineSegment(sketch, "E222", {"start": v(0, 0) * mm, "end": v(194.56, 0) * mm, "construction": true});
            skLineSegment(sketch, "E223.bottom", {"start": v(11.46, -88.9) * mm, "end": v(177.8, -88.9) * mm});
            skLineSegment(sketch, "E223.top", {"start": v(11.46, 88.9) * mm, "end": v(177.8, 88.9) * mm});
            skLineSegment(sketch, "E223.left", {"start": v(5.11, -82.55) * mm, "end": v(5.1, 82.55) * mm});
            skLineSegment(sketch, "E223.right", {"start": v(184.15, -82.55) * mm, "end": v(184.15, 82.55) * mm});
            skPoint(sketch, "E224.visualSharp", {"position": v(184.15, 88.9) * mm});
            skArc(sketch, "E224.filletArc", {"start": v(184.15, 82.55) * mm, "mid": v(182.3, 87.04) * mm, "end": v(177.8, 88.9) * mm});
            skPoint(sketch, "E225.visualSharp", {"position": v(184.15, -88.9) * mm});
            skArc(sketch, "E225.filletArc", {"start": v(177.8, -88.9) * mm, "mid": v(182.3, -87.04) * mm, "end": v(184.15, -82.55) * mm});
            skPoint(sketch, "E226.visualSharp", {"position": v(5.11, -88.9) * mm});
            skArc(sketch, "E226.filletArc", {"start": v(5.11, -82.55) * mm, "mid": v(6.97, -87.04) * mm, "end": v(11.46, -88.9) * mm});
            skPoint(sketch, "E227.visualSharp", {"position": v(5.1, 88.9) * mm});
            skArc(sketch, "E227.filletArc", {"start": v(11.46, 88.9) * mm, "mid": v(6.97, 87.04) * mm, "end": v(5.1, 82.55) * mm});
            skCircle(sketch, "E228", {"center": v(94.68, 0) * mm, "radius": 12.7 * mm});
            skSolve(sketch);
        }
        {
            var Q0;
            Q0 = qSketchRegion(id + "F10", true);
            extrude(context, id + "F11", {"entities" : qUnion([Q0]), "depth" : 3.17 * mm});
        }
        {
            var Q0;
            Q0=makeQuery(id+"F9.opExtrude","SWEPT_FACE",FACE,{"disambiguationData":[OSD([sQuery(id+"F8.wireOp",EDGE,"E211.bottom")])]});
            var sketch = newSketch(context, id + "F12", { "sketchPlane" : qUnion([Q0])});
            skPoint(sketch, "E229.endSnap0", {"position": v(96.89, -85.72) * mm});
            skLineSegment(sketch, "E230.bottom", {"start": v(13.05, -88.9) * mm, "end": v(178.15, -88.9) * mm});
            skLineSegment(sketch, "E230.top", {"start": v(13.05, 88.9) * mm, "end": v(178.15, 88.9) * mm});
            skLineSegment(sketch, "E230.left", {"start": v(6.7, -82.55) * mm, "end": v(6.7, 82.55) * mm});
            skLineSegment(sketch, "E230.right", {"start": v(184.5, -82.55) * mm, "end": v(184.5, 82.55) * mm});
            skPoint(sketch, "E231.visualSharp", {"position": v(184.5, 88.9) * mm});
            skArc(sketch, "E231.filletArc", {"start": v(184.5, 82.55) * mm, "mid": v(182.64, 87.04) * mm, "end": v(178.15, 88.9) * mm});
            skPoint(sketch, "E232.visualSharp", {"position": v(184.5, -88.9) * mm});
            skArc(sketch, "E232.filletArc", {"start": v(178.15, -88.9) * mm, "mid": v(182.64, -87.04) * mm, "end": v(184.5, -82.55) * mm});
            skPoint(sketch, "E233.visualSharp", {"position": v(6.7, -88.9) * mm});
            skArc(sketch, "E233.filletArc", {"start": v(6.7, -82.55) * mm, "mid": v(8.56, -87.04) * mm, "end": v(13.05, -88.9) * mm});
            skPoint(sketch, "E234.visualSharp", {"position": v(6.7, 88.9) * mm});
            skArc(sketch, "E234.filletArc", {"start": v(13.05, 88.9) * mm, "mid": v(8.56, 87.04) * mm, "end": v(6.7, 82.55) * mm});
            skArc(sketch, "E235", {"start": v(113.09, 45.03) * mm, "mid": v(32.58, -59.85) * mm, "end": v(137.45, 20.67) * mm});
            skLineSegment(sketch, "E236", {"start": v(160.6, 68.17) * mm, "end": v(79.72, -12.7) * mm, "construction": true});
            skLineSegment(sketch, "E237", {"start": v(138.96, 32.17) * mm, "end": v(171.67, 64.88) * mm});
            skLineSegment(sketch, "E238", {"start": v(124.6, 46.54) * mm, "end": v(157.3, 79.25) * mm});
            skLineSegment(sketch, "E239", {"start": v(170.77, 79.25) * mm, "end": v(171.67, 78.35) * mm});
            skPoint(sketch, "E240.visualSharp", {"position": v(164.04, 85.98) * mm});
            skArc(sketch, "E240.filletArc", {"start": v(170.77, 79.25) * mm, "mid": v(164.04, 82.04) * mm, "end": v(157.3, 79.25) * mm});
            skPoint(sketch, "E241.visualSharp", {"position": v(178.4, 71.61) * mm});
            skArc(sketch, "E241.filletArc", {"start": v(171.67, 64.88) * mm, "mid": v(174.46, 71.61) * mm, "end": v(171.67, 78.35) * mm});
            skPoint(sketch, "E242.visualSharp", {"position": v(133.5, 26.71) * mm});
            skArc(sketch, "E242.filletArc", {"start": v(138.96, 32.17) * mm, "mid": v(136.25, 26.67) * mm, "end": v(137.45, 20.67) * mm});
            skPoint(sketch, "E243.visualSharp", {"position": v(119.13, 41.08) * mm});
            skArc(sketch, "E243.filletArc", {"start": v(113.09, 45.03) * mm, "mid": v(119.1, 43.83) * mm, "end": v(124.6, 46.54) * mm});
            skSolve(sketch);
        }
        {
            var Q0;
            Q0 = qSketchRegion(id + "F12", true);
            extrude(context, id + "F13", {"entities" : qUnion([Q0]), "depth" : 3.17 * mm});
        }
        {
            var Q0;
            Q0=makeQuery(id+"F9.opExtrude","SWEPT_FACE",FACE,{"disambiguationData":[OSD([sQuery(id+"F8.wireOp",EDGE,"E211.bottom")])]});
            var sketch = newSketch(context, id + "F14", { "sketchPlane" : qUnion([Q0])});
            skLineSegment(sketch, "E244", {"start": v(102.1, -119.9) * mm, "end": v(102.1, 64.58) * mm, "construction": true});
            skPoint(sketch, "E244.endSnap0", {"position": v(102.1, -119.9) * mm});
            skLineSegment(sketch, "E245", {"start": v(6.78, -33.54) * mm, "end": v(201.34, -33.54) * mm, "construction": true});
            skLineSegment(sketch, "E246.bottom", {"start": v(19.55, -122.44) * mm, "end": v(184.65, -122.44) * mm});
            skLineSegment(sketch, "E246.top", {"start": v(19.55, 55.36) * mm, "end": v(184.65, 55.36) * mm});
            skLineSegment(sketch, "E246.left", {"start": v(13.2, -116.09) * mm, "end": v(13.2, 49.01) * mm});
            skLineSegment(sketch, "E246.right", {"start": v(191, -116.09) * mm, "end": v(191, 49.01) * mm});
            skPoint(sketch, "E247.visualSharp", {"position": v(191, 55.36) * mm});
            skArc(sketch, "E247.filletArc", {"start": v(191, 49.01) * mm, "mid": v(189.14, 53.5) * mm, "end": v(184.65, 55.36) * mm});
            skPoint(sketch, "E248.visualSharp", {"position": v(191, -122.44) * mm});
            skArc(sketch, "E248.filletArc", {"start": v(184.65, -122.44) * mm, "mid": v(189.14, -120.58) * mm, "end": v(191, -116.09) * mm});
            skPoint(sketch, "E249.visualSharp", {"position": v(13.2, -122.44) * mm});
            skArc(sketch, "E249.filletArc", {"start": v(13.2, -116.09) * mm, "mid": v(15.06, -120.58) * mm, "end": v(19.55, -122.44) * mm});
            skPoint(sketch, "E250.visualSharp", {"position": v(13.2, 55.36) * mm});
            skArc(sketch, "E250.filletArc", {"start": v(19.55, 55.36) * mm, "mid": v(15.06, 53.5) * mm, "end": v(13.2, 49.01) * mm});
            skCircle(sketch, "E251", {"center": v(145.92, 10.28) * mm, "radius": 41.91 * mm});
            skCircle(sketch, "E252.0.1.0", {"center": v(145.92, -78.62) * mm, "radius": 41.91 * mm});
            skCircle(sketch, "E252.1.0.0", {"center": v(57.02, 10.28) * mm, "radius": 41.91 * mm});
            skCircle(sketch, "E252.1.1.0", {"center": v(57.02, -78.62) * mm, "radius": 41.91 * mm});
            skLineSegment(sketch, "E252.direction1", {"start": v(145.92, 10.28) * mm, "end": v(57.02, 10.28) * mm, "construction": true});
            skLineSegment(sketch, "E252.direction2", {"start": v(145.92, 10.28) * mm, "end": v(145.92, -78.62) * mm, "construction": true});
            skSolve(sketch);
        }
        {
            var Q0;
            Q0 = qSketchRegion(id + "F14", true);
            extrude(context, id + "F15", {"entities" : qUnion([Q0]), "depth" : 3.17 * mm});
        }
        {
            var Q0;
            Q0=makeQuery(id+"F9.opExtrude","SWEPT_FACE",FACE,{"disambiguationData":[OSD([sQuery(id+"F8.wireOp",EDGE,"E211.bottom")])]});
            var sketch = newSketch(context, id + "F16", { "sketchPlane" : qUnion([Q0])});
            skLineSegment(sketch, "E253", {"start": v(96.89, -82.55) * mm, "end": v(96.89, 101.93) * mm, "construction": true});
            skPoint(sketch, "E253.endSnap0", {"position": v(96.89, -82.55) * mm});
            skLineSegment(sketch, "E254", {"start": v(1.59, 3.18) * mm, "end": v(196.15, 3.18) * mm, "construction": true});
            skLineSegment(sketch, "E255.bottom", {"start": v(14.29, -85.72) * mm, "end": v(179.39, -85.72) * mm});
            skLineSegment(sketch, "E255.top", {"start": v(14.29, 92.08) * mm, "end": v(179.39, 92.08) * mm});
            skLineSegment(sketch, "E255.left", {"start": v(7.94, -79.38) * mm, "end": v(7.94, 85.73) * mm});
            skLineSegment(sketch, "E255.right", {"start": v(185.74, -79.37) * mm, "end": v(185.74, 85.73) * mm});
            skPoint(sketch, "E256.visualSharp", {"position": v(185.74, 92.08) * mm});
            skArc(sketch, "E256.filletArc", {"start": v(185.74, 85.73) * mm, "mid": v(183.88, 90.22) * mm, "end": v(179.39, 92.08) * mm});
            skPoint(sketch, "E257.visualSharp", {"position": v(185.74, -85.72) * mm});
            skArc(sketch, "E257.filletArc", {"start": v(179.39, -85.72) * mm, "mid": v(183.88, -83.87) * mm, "end": v(185.74, -79.38) * mm});
            skPoint(sketch, "E258.visualSharp", {"position": v(7.94, -85.72) * mm});
            skArc(sketch, "E258.filletArc", {"start": v(7.94, -79.38) * mm, "mid": v(9.8, -83.87) * mm, "end": v(14.29, -85.72) * mm});
            skPoint(sketch, "E259.visualSharp", {"position": v(7.94, 92.08) * mm});
            skArc(sketch, "E259.filletArc", {"start": v(14.29, 92.08) * mm, "mid": v(9.8, 90.22) * mm, "end": v(7.94, 85.73) * mm});
            skCircle(sketch, "E260", {"center": v(60.64, 39.37) * mm, "radius": 46.35 * mm});
            skCircle(sketch, "E261", {"center": v(133.03, -33.02) * mm, "radius": 46.35 * mm});
            skSolve(sketch);
        }
        {
            var Q0;
            Q0 = qSketchRegion(id + "F16", true);
            extrude(context, id + "F17", {"entities" : qUnion([Q0]), "depth" : 3.17 * mm});
        }
    });
